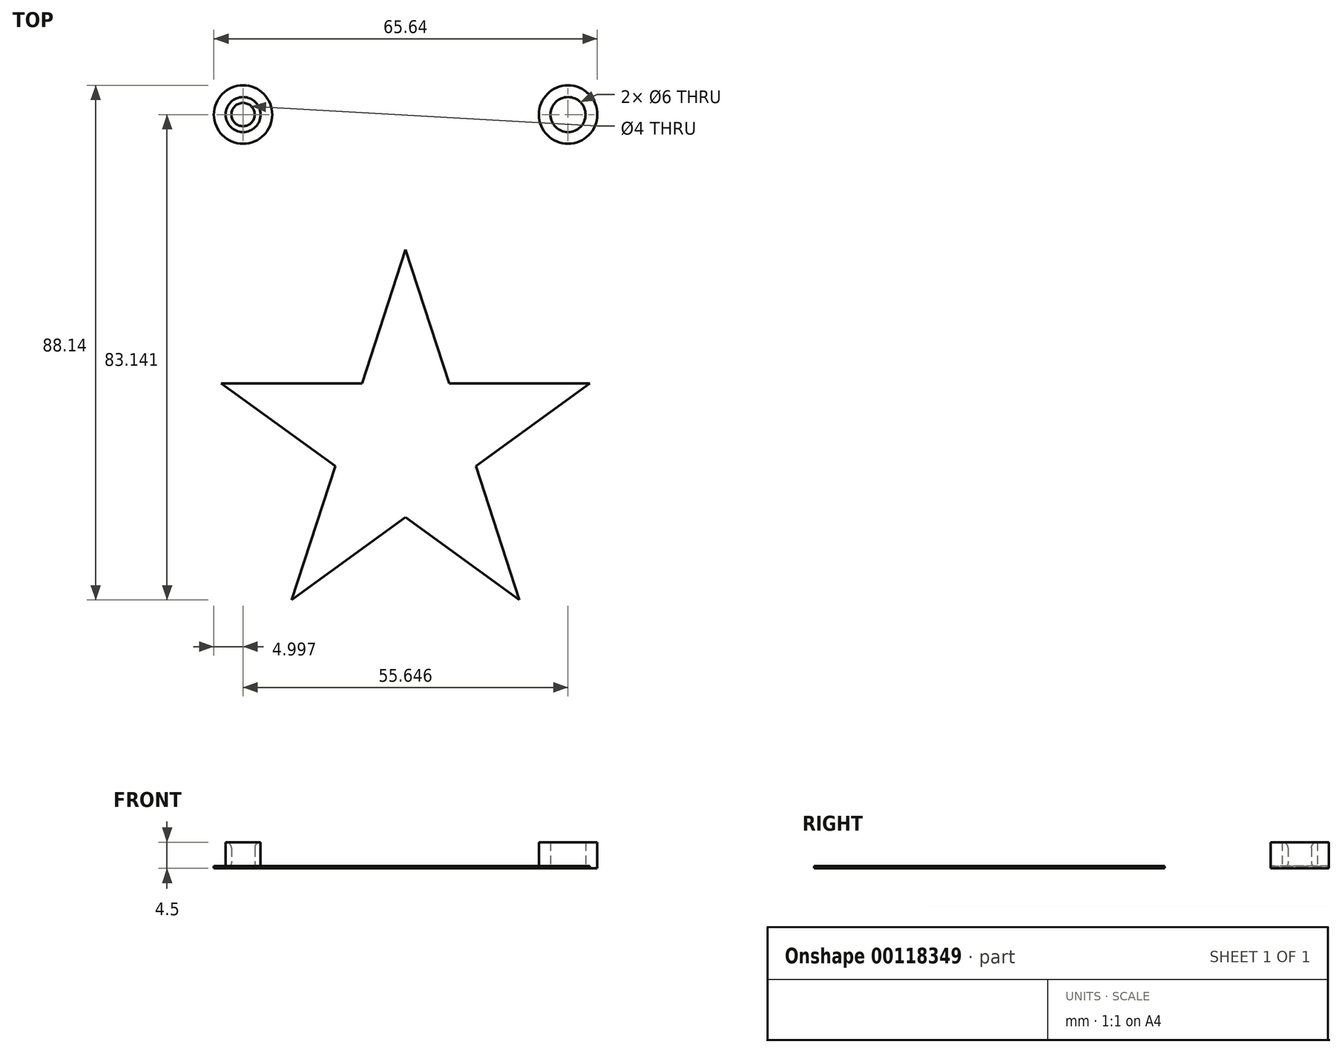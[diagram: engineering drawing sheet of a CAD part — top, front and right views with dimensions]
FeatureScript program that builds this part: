
annotation { "Feature Type Name" : "Feature", "Feature Type Description" : "" }
export const myFeature = defineFeature(function(context is Context, id is Id, definition is map)
    precondition{}
    {
        {
            var Q0;
            Q0=qCreatedBy(makeId("Top.planeOp"),FACE);
            var sketch = newSketch(context, id + "F0", { "sketchPlane" : qUnion([Q0])});
            skCircle(sketch, "E0", {"center": v(-27.82, 20.3) * mm, "radius": 2 * mm});
            skCircle(sketch, "E1", {"center": v(-27.82, 20.3) * mm, "radius": 5 * mm});
            skCircle(sketch, "E2", {"center": v(-27.82, 20.3) * mm, "radius": 3 * mm});
            skCircle(sketch, "E3.MirrorC", {"center": v(27.82, 20.3) * mm, "radius": 5 * mm});
            skCircle(sketch, "E4.MirrorC", {"center": v(27.82, 20.3) * mm, "radius": 3 * mm});
            skCircle(sketch, "E5.MirrorC", {"center": v(27.82, 20.3) * mm, "radius": 2 * mm});
            skSolve(sketch);
        }
        {
            var Q0;
            Q0=makeQuery(id+"F0.imprint","IMPRINT",FACE,{"disambiguationData":[TD([[makeQuery(id+"F0.imprint","IMPRINT",EDGE,{"derivedFrom":sQuery(id+"F0.wireOp",EDGE,"E1")}),1.0]])]});
            var Q1;
            Q1=makeQuery(id+"F0.imprint","IMPRINT",FACE,{"disambiguationData":[TD([[makeQuery(id+"F0.imprint","IMPRINT",EDGE,{"derivedFrom":sQuery(id+"F0.wireOp",EDGE,"E3.MirrorC")}),-1.0]])]});
            extrude(context, id + "F1", {"entities" : qUnion([Q0, Q1]), "depth" : .4 * mm});
        }
        {
            var Q0;
            Q0=makeQuery(id+"F0.imprint","IMPRINT",FACE,{"disambiguationData":[TD([[makeQuery(id+"F0.imprint","IMPRINT",EDGE,{"derivedFrom":sQuery(id+"F0.wireOp",EDGE,"E0")}),-1.0]])]});
            var Q1;
            Q1=makeQuery(id+"F0.imprint","IMPRINT",FACE,{"disambiguationData":[TD([[makeQuery(id+"F0.imprint","IMPRINT",EDGE,{"derivedFrom":sQuery(id+"F0.wireOp",EDGE,"E4.MirrorC")}),-1.0]])]});
            extrude(context, id + "F2", {"entities" : qUnion([Q0, Q1]), "depth" : 4.5 * mm});
        }
        {
            var Q0;
            Q0=makeQuery(id+"F2.opExtrude","CAP_EDGE",EDGE,{"disambiguationData":[OSD([sQuery(id+"F0.wireOp",EDGE,"E0")])],"isStart":false});
            var Q1;
            Q1=makeQuery(id+"F2.opExtrude","CAP_EDGE",EDGE,{"disambiguationData":[OSD([sQuery(id+"F0.wireOp",EDGE,"E0")])],"isStart":true});
            var Q2;
            Q2=makeQuery(id+"F2.opExtrude","CAP_EDGE",EDGE,{"disambiguationData":[OSD([sQuery(id+"F0.wireOp",EDGE,"E5.MirrorC")])],"isStart":false});
            var Q3;
            Q3=makeQuery(id+"F2.opExtrude","CAP_EDGE",EDGE,{"disambiguationData":[OSD([sQuery(id+"F0.wireOp",EDGE,"E5.MirrorC")])],"isStart":true});
            fillet(context, id + "F3", {"entities" : qUnion([Q0, Q1, Q2, Q3]), "radius" : 1 * mm, "tangentPropagation" : true, "allowEdgeOverflow" : false});
        }
        {
            var Q0;
            Q0=qCreatedBy(makeId("Top.planeOp"),FACE);
            var sketch = newSketch(context, id + "F4", { "sketchPlane" : qUnion([Q0])});
            skLineSegment(sketch, "E6.MirrorCS", {"start": v(12.05, -39.93) * mm, "end": v(7.45, -25.76) * mm, "construction": true});
            skLineSegment(sketch, "E7.MirrorCS", {"start": v(7.45, -25.76) * mm, "end": v(-7.45, -25.76) * mm, "construction": true});
            skLineSegment(sketch, "E8.MirrorCS", {"start": v(-12.05, -39.93) * mm, "end": v(-19.5, -62.85) * mm});
            skLineSegment(sketch, "E9.MirrorCS", {"start": v(-7.45, -25.76) * mm, "end": v(0, -2.85) * mm});
            skLineSegment(sketch, "E10.MirrorCS", {"start": v(31.54, -25.76) * mm, "end": v(7.45, -25.76) * mm});
            skLineSegment(sketch, "E11.MirrorCS", {"start": v(12.05, -39.93) * mm, "end": v(31.54, -25.76) * mm});
            skLineSegment(sketch, "E12.MirrorCS", {"start": v(12.05, -39.93) * mm, "end": v(19.5, -62.85) * mm});
            skLineSegment(sketch, "E13.MirrorCS", {"start": v(19.5, -62.85) * mm, "end": v(0, -48.68) * mm});
            skLineSegment(sketch, "E14.MirrorCS", {"start": v(-31.54, -25.76) * mm, "end": v(-12.05, -39.93) * mm});
            skLineSegment(sketch, "E15.MirrorCS", {"start": v(-7.45, -25.76) * mm, "end": v(-31.54, -25.76) * mm});
            skPoint(sketch, "E16.MirrorP", {"position": v(0, -36.01) * mm});
            skLineSegment(sketch, "E17.MirrorCS", {"start": v(0, -2.85) * mm, "end": v(7.45, -25.76) * mm});
            skLineSegment(sketch, "E18.MirrorCS", {"start": v(-7.45, -25.76) * mm, "end": v(-12.05, -39.93) * mm, "construction": true});
            skLineSegment(sketch, "E19.MirrorCS", {"start": v(-19.5, -62.85) * mm, "end": v(0, -48.68) * mm});
            skLineSegment(sketch, "E20.MirrorCS", {"start": v(-12.05, -39.93) * mm, "end": v(0, -48.68) * mm, "construction": true});
            skLineSegment(sketch, "E21.MirrorCS", {"start": v(0, -48.68) * mm, "end": v(12.05, -39.93) * mm, "construction": true});
            skPoint(sketch, "E22.MirrorP", {"position": v(9.75, -32.85) * mm});
            skSolve(sketch);
        }
        {
            var Q0;
            Q0=makeQuery(id+"F4.imprint","IMPRINT",FACE,{"disambiguationData":[TD([[makeQuery(id+"F4.imprint","IMPRINT",EDGE,{"derivedFrom":sQuery(id+"F4.wireOp",EDGE,"E8.MirrorCS")}),1.0]])]});
            extrude(context, id + "F5", {"entities" : qUnion([Q0]), "depth" : .4 * mm});
        }
        {
            var Q0;
            Q0=makeQuery(id+"F5.opExtrude","CAP_FACE",FACE,{"disambiguationData":[OSD([sQuery(id+"F4.wireOp",EDGE,"E8.MirrorCS"),sQuery(id+"F4.wireOp",EDGE,"E9.MirrorCS"),sQuery(id+"F4.wireOp",EDGE,"E10.MirrorCS"),sQuery(id+"F4.wireOp",EDGE,"E11.MirrorCS"),sQuery(id+"F4.wireOp",EDGE,"E12.MirrorCS"),sQuery(id+"F4.wireOp",EDGE,"E13.MirrorCS"),sQuery(id+"F4.wireOp",EDGE,"E14.MirrorCS"),sQuery(id+"F4.wireOp",EDGE,"E15.MirrorCS"),sQuery(id+"F4.wireOp",EDGE,"E17.MirrorCS"),sQuery(id+"F4.wireOp",EDGE,"E19.MirrorCS")])],"isStart":false});
            var sketch = newSketch(context, id + "F6", { "sketchPlane" : qUnion([Q0])});
            skLineSegment(sketch, "E23", {"start": v(7.45, -25.76) * mm, "end": v(12.05, -39.93) * mm});
            skLineSegment(sketch, "E24", {"start": v(31.54, -25.76) * mm, "end": v(9.75, -32.85) * mm});
            skPoint(sketch, "E25", {"position": v(15.25, -31.06) * mm});
            skSolve(sketch);
        }
        {
            var Q0;
            Q0=sQuery(id+"F6.wireOp",EDGE,"E24");
            cPlane(context, id + "F7", {"entities" : qUnion([Q0]), "cplaneType" : CPlaneType.LINE_ANGLE, "offset" : 25 * mm, "angle" : 0 * degree, "width" : 150 * mm, "height" : 150 * mm});
        }
    });
